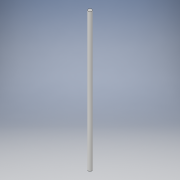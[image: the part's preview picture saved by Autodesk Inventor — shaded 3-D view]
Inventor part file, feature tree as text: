
AUTODESK INVENTOR PART (.ipt)
format: ipt  version: 2019 (Build 230136000, 136)  size: 89,600 bytes
history: native  units: mm
features: extrude x1, sketch x1
ambient origin geometry x8: Origin, YZ Plane, XZ Plane, XY Plane, X Axis, Y Axis, Z Axis, Center Point
bodies: Solid1 (feature_tree)
feature tree (2):
  extrude  "Extrusion1"  Depth=565.0mm TaperAngle=0.0deg
  sketch  "Sketch1"  dims[d0=15.0mm d1=565.0mm d2=0.0mm]
